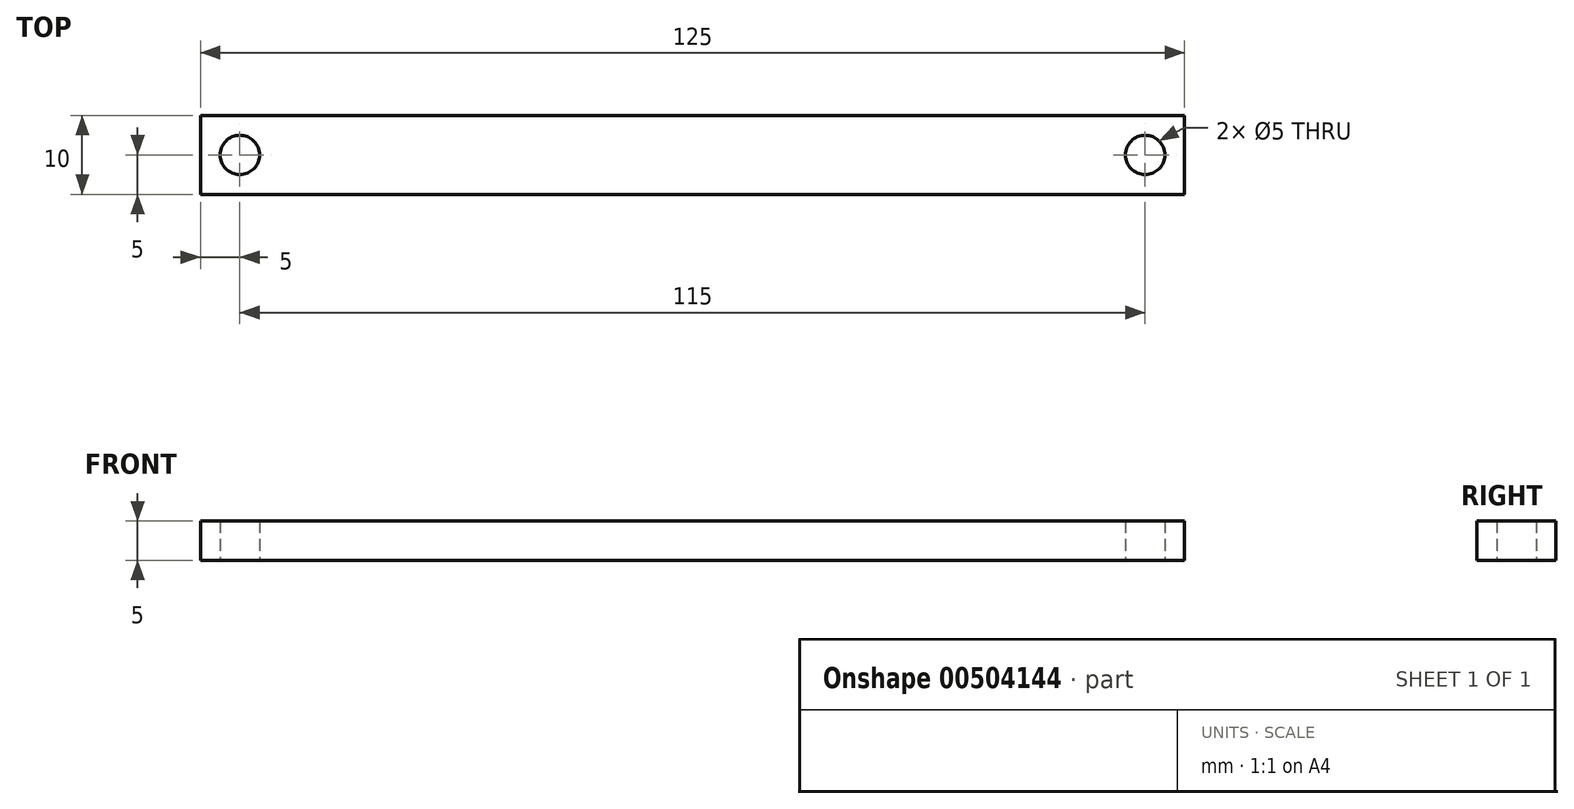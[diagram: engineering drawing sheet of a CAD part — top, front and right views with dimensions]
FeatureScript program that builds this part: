
annotation { "Feature Type Name" : "Feature", "Feature Type Description" : "" }
export const myFeature = defineFeature(function(context is Context, id is Id, definition is map)
    precondition{}
    {
        {
            var Q0;
            Q0=qCreatedBy(makeId("Top.planeOp"),FACE);
            var sketch = newSketch(context, id + "F0", { "sketchPlane" : qUnion([Q0])});
            skLineSegment(sketch, "E0.bottom", {"start": v(0, 0) * mm, "end": v(125, 0) * mm});
            skLineSegment(sketch, "E0.top", {"start": v(0, 10) * mm, "end": v(125, 10) * mm});
            skLineSegment(sketch, "E0.left", {"start": v(0, 0) * mm, "end": v(0, 10) * mm});
            skLineSegment(sketch, "E0.right", {"start": v(125, 0) * mm, "end": v(125, 10) * mm});
            skCircle(sketch, "E1", {"center": v(5, 5) * mm, "radius": 2.5 * mm});
            skPoint(sketch, "E1.centerSnap0", {"position": v(0, 5) * mm});
            skCircle(sketch, "E2", {"center": v(120, 5) * mm, "radius": 2.5 * mm});
            skPoint(sketch, "E2.centerSnap0", {"position": v(125, 5) * mm});
            skSolve(sketch);
        }
        {
            var Q0;
            Q0 = qSketchRegion(id + "F0", true);
            extrude(context, id + "F1", {"entities" : qUnion([Q0]), "depth" : 5 * mm, "offsetDistance" : 25 * mm});
        }
    });
